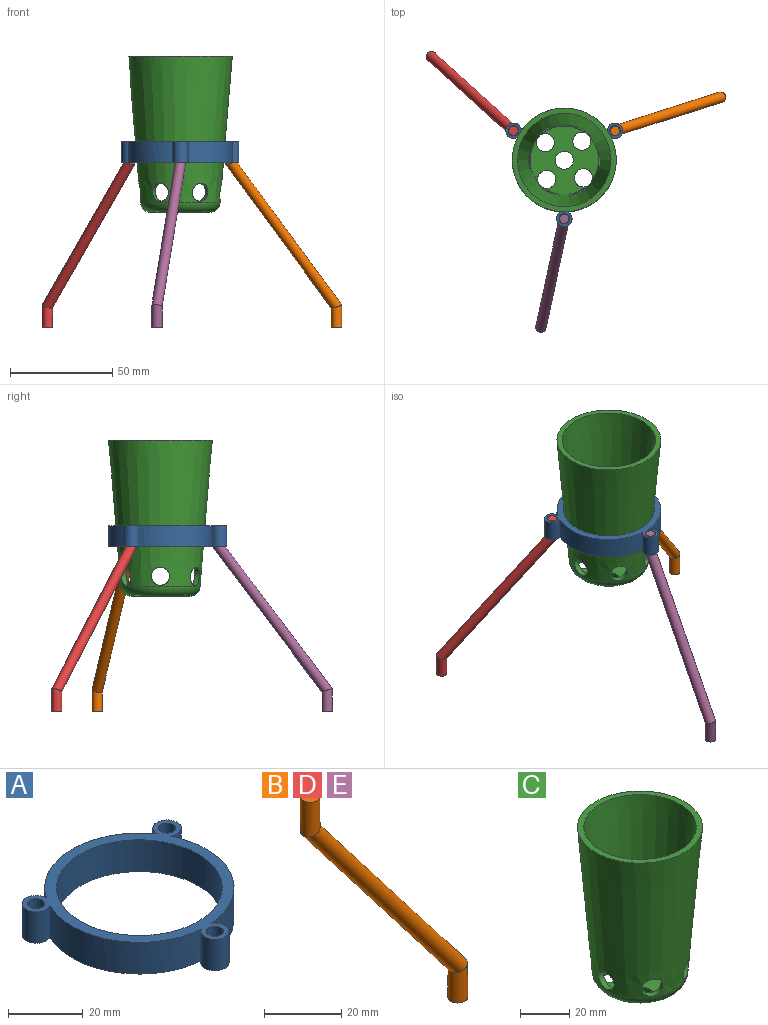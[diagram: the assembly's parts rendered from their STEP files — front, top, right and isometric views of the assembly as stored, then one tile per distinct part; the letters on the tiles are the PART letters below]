
ASSEMBLY  parts=5 mates=2
PART A: 13 faces, bbox 57.2x57.9x10.4 mm
  f0: cylinder r=22.23mm len=44.45mm, axis (0,0,1), area 1454.3mm2, adj f2,f3
  f1: cylinder r=25.4mm len=50.8mm, axis (0,0,1), area 1545.7mm2, adj f2,f3,f5,f6,f8,f9,f11,f12
  f2: plane 50.8x50.8mm, normal (0,0,-1), area 475mm2, adj f0,f1
  f3: plane 57.86x57.24mm, normal (0,0,1), area 558.3mm2, adj f0,f1,f4,f5,f7,f8,f10,f11
  f4: cylinder r=2.29mm len=10.31mm, axis (0,0,1), area 148.1mm2, adj f3,f6
  f5: cylinder r=3.81mm len=10.31mm, axis (0,0,1), area 206.4mm2, adj f1,f3,f6
  f6: plane 7.62x7.62mm, normal (0,0,-1), area 27.8mm2, adj f1,f4,f5
  f7: cylinder r=2.29mm len=10.31mm, axis (0,0,1), area 148.1mm2, adj f3,f9
  f8: cylinder r=3.81mm len=10.31mm, axis (0,0,1), area 206.4mm2, adj f1,f3,f9
  f9: plane 7.62x7.13mm, normal (0,0,-1), area 27.8mm2, adj f1,f7,f8
  f10: cylinder r=2.29mm len=10.31mm, axis (0,0,1), area 148.1mm2, adj f3,f12
  f11: cylinder r=3.81mm len=10.31mm, axis (0,0,1), area 206.4mm2, adj f1,f3,f12
  f12: plane 7.62x7.62mm, normal (0,0,-1), area 27.8mm2, adj f1,f10,f11
PART B: 5 faces, bbox 59.2x5.1x90.8 mm
  f0: plane 5.08x5.08mm, normal (0,0,-1), area 20.3mm2, adj f2
  f1: plane 5.08x5.08mm, normal (0,0,1), area 20.3mm2, adj f4
  f2: cylinder r=2.54mm len=11.18mm, axis (0,0,-1), area 164.6mm2, adj f0,f3
  f3: cylinder r=2.54mm len=74.68mm, axis (0.61,0,-0.79), area 1414.9mm2, adj f2,f4
  f4: cylinder r=2.54mm len=11.18mm, axis (0,0,-1), area 164.6mm2, adj f1,f3
PART C: 21 faces, bbox 50.8x50.8x76.2 mm
  f0: cylinder r=4.45mm len=9.48mm, axis (0.5,0.87,0), area 72.2mm2, adj f12,f14
  f1: cylinder r=4.45mm len=9.48mm, axis (-0.5,0.87,0), area 72.2mm2, adj f12,f14
  f2: cylinder r=4.45mm len=8.89mm, axis (-1,0,0), area 72.2mm2, adj f12,f14
  f3: cylinder r=4.45mm len=9.48mm, axis (-0.5,-0.87,0), area 72.2mm2, adj f12,f14
  f4: cylinder r=4.45mm len=9.48mm, axis (0.5,-0.87,0), area 72.2mm2, adj f12,f14
  f5: cylinder r=4.45mm len=8.89mm, axis (0,0,-1), area 77.9mm2, adj f6,f13,f14,f15,f20
  f6: plane 1.86x1.71mm, normal (0,0,-1), area 0.2mm2, adj f5,f14
  f7: cylinder r=4.45mm len=8.89mm, axis (0,0,-1), area 77.9mm2, adj f8,f13,f14,f15,f20
  f8: plane 1.86x1.71mm, normal (0,0,-1), area 0.2mm2, adj f7,f14
  f9: cylinder r=4.45mm len=8.89mm, axis (0,0,-1), area 77.9mm2, adj f10,f13,f14,f15,f20
  f10: plane 1.86x1.71mm, normal (0,0,-1), area 0.2mm2, adj f9,f14
  f11: plane 50.8x50.8mm, normal (0,0,1), area 386.4mm2, adj f12,f14
  f12: cone r=25.4mm half-angle=4.8deg, axis (0,0,1), area 9736.2mm2, adj f0,f1,f2,f3,f4,f11,f19,f20
  f13: plane 28.75x28.75mm, normal (0,0,-1), area 411.3mm2, adj f5,f7,f9,f17,f18,f20
  f14: cone r=22.87mm half-angle=4.8deg, axis (0,0,1), area 8764.1mm2, adj f0,f1,f2,f3,f4,f5,f6,f7
  f15: plane 33.43x33.43mm, normal (0,0,1), area 571.9mm2, adj f5,f7,f9,f14,f17,f18
  f16: plane 1.86x1.71mm, normal (0,0,-1), area 0.2mm2, adj f14,f17
  f17: cylinder r=4.45mm len=8.89mm, axis (0,0,-1), area 77.9mm2, adj f13,f14,f15,f16,f20
  f18: cylinder r=4.45mm len=8.89mm, axis (0,0,-1), area 70.9mm2, adj f13,f15
  f19: cylinder r=4.45mm len=8.89mm, axis (1,0,0), area 72.2mm2, adj f12,f14
  f20: torus R=14.38mm, axis (0,0,-1), area 756mm2, adj f5,f7,f9,f12,f13,f17
PART D: same geometry as B
PART E: same geometry as B
PLACE A t=(-39.94,-6.35,25.65)mm fixed
PLACE B rot(axis=(0,0,1),17.8deg) t=(9.05,15.74,25.65)mm
PLACE C t=(-39.94,-6.35,10.42)mm
PLACE D rot(axis=(0,0,1),137.8deg) t=(-83.56,25.04,25.65)mm
PLACE E rot(axis=(0,0,-1),102.2deg) t=(-45.31,-59.82,25.65)mm
MATE cylindrical C.f12 <-> A.f0  axis (0,0,1) through (-39.94,-6.35,67.31)mm
MATE revolute A.f10 <-> B.f4  axis (0,0,1) through (-15.13,7.98,25.65)mm
